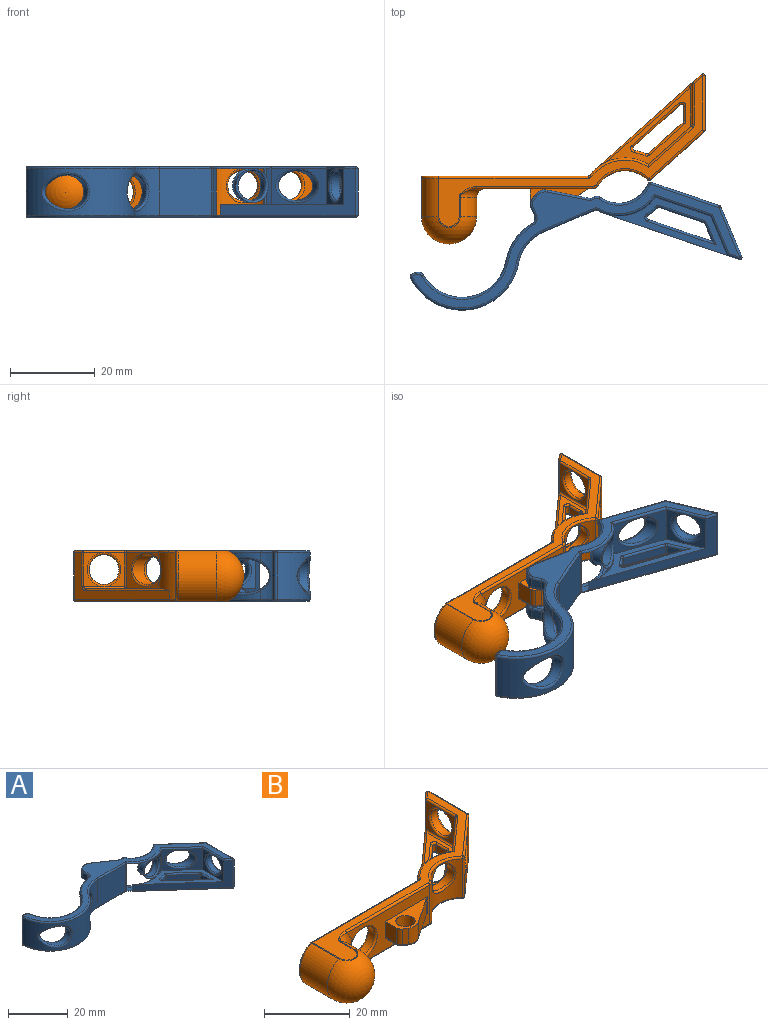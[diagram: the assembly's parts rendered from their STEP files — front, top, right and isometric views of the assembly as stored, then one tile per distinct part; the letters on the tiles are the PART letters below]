
ASSEMBLY  parts=2 mates=1
PART A: 142 faces, bbox 75.2x33.9x12.5 mm
  f0: plane 72.76x32.31mm, normal (0,0,-1), area 331.1mm2, adj f1,f2,f3,f4,f5,f6,f7,f8
  f1: torus R=12mm, axis (0,0,-1), area 2.2mm2, adj f0,f2,f7,f29
  f2: torus R=1mm, axis (0,0,-1), area 1.2mm2, adj f0,f1,f3,f30
  f3: cylinder r=0.5mm len=13.02mm, axis (0.75,-0.67,0), area 12.8mm2, adj f0,f2,f4,f31
  f4: cylinder r=0.5mm len=5.59mm, axis (0,1,0), area 3.8mm2, adj f0,f3,f5,f32
  f5: torus R=1mm, axis (0,0,-1), area 0.5mm2, adj f0,f4,f6,f33
  f6: cylinder r=0.5mm len=8.55mm, axis (-0.75,0.67,0), area 8.7mm2, adj f0,f5,f7,f34
  f7: torus R=1mm, axis (0,0,-1), area 0.6mm2, adj f0,f1,f6,f35
  f8: torus R=12.5mm, axis (0,0,-1), area 8.5mm2, adj f0,f9,f28,f36
  f9: torus R=2mm, axis (0,0,-1), area 1.9mm2, adj f0,f8,f10,f37
  f10: cylinder r=0.5mm len=2.34mm, axis (0,1,0), area 1.8mm2, adj f0,f9,f11,f38
  f11: torus R=1mm, axis (0,0,-1), area 1mm2, adj f0,f10,f12,f39
  f12: cylinder r=0.5mm len=1.44mm, axis (0.83,0.56,0), area 1.1mm2, adj f0,f11,f13,f40
  f13: torus R=2.5mm, axis (0,0,-1), area 2.6mm2, adj f0,f12,f14,f41
  f14: cylinder r=0.5mm len=8.86mm, axis (0.83,-0.56,0), area 8.1mm2, adj f0,f13,f15,f42
  f15: cylinder r=0.5mm len=1.22mm, axis (-1,0,0), area 0.9mm2, adj f0,f14,f16,f43
  f16: torus R=1mm, axis (0,0,-1), area 1.1mm2, adj f0,f15,f17,f44
  f17: torus R=8mm, axis (0,0,-1), area 10.8mm2, adj f0,f16,f45,f46
  f18: cylinder r=0.5mm len=13.04mm, axis (-0.75,0.67,0), area 13.4mm2, adj f0,f45,f47,f48
  f19: cylinder r=0.5mm len=12.75mm, axis (0,-1,0), area 10mm2, adj f0,f47,f49,f50
  f20: cylinder r=0.5mm len=25.33mm, axis (-0.75,0.67,0), area 26.3mm2, adj f0,f21,f49,f51
  f21: torus R=10mm, axis (0,0,-1), area 1.5mm2, adj f0,f20,f22,f52
  f22: torus R=1mm, axis (0,0,-1), area 0.5mm2, adj f0,f21,f23,f53
  f23: cylinder r=0.5mm len=13.18mm, axis (1,0,0), area 10.3mm2, adj f0,f22,f24,f54
  f24: torus R=10.5mm, axis (0,0,-1), area 7.9mm2, adj f0,f23,f25,f55
  f25: torus R=13mm, axis (0,0,-1), area 26.3mm2, adj f0,f24,f56,f57
  f26: cylinder r=0.5mm len=1.08mm, axis (-1,0,0), area 0.9mm2, adj f0,f27,f57,f58
  f27: torus R=1mm, axis (0,0,-1), area 1.5mm2, adj f0,f26,f28,f59
  f28: torus R=11mm, axis (0,0,-1), area 20.4mm2, adj f0,f8,f27,f60
  f29: cylinder r=12.5mm len=2.7mm, axis (0,0,1), area 5.7mm2, adj f1,f30,f35,f61
  f30: cylinder r=0.5mm len=2mm, axis (0,0,1), area 2.2mm2, adj f2,f29,f31,f62
  f31: plane 11.86x10.6mm, normal (0.67,0.75,0), area 31.8mm2, adj f3,f30,f32,f63
  f32: plane 4.47x2mm, normal (-1,0,0), area 8.9mm2, adj f4,f31,f33,f64
  f33: cylinder r=0.5mm len=2mm, axis (0,0,-1), area 0.8mm2, adj f5,f32,f34,f65
  f34: plane 8.21x7.35mm, normal (-0.67,-0.75,0), area 22mm2, adj f6,f33,f35,f66
  f35: cylinder r=0.5mm len=2mm, axis (0,0,1), area 1.1mm2, adj f7,f29,f34,f67
  f36: cylinder r=13mm len=11mm, axis (0,0,1), area 57.8mm2, adj f8,f37,f43,f60,f68,f69,f70,f71
  f37: cylinder r=1.5mm len=2.25mm, axis (0,0,1), area 4.8mm2, adj f9,f36,f38,f74
  f38: plane 2.34x2.25mm, normal (-1,0,0), area 5.3mm2, adj f10,f37,f39,f75
  f39: cylinder r=1.5mm len=2.25mm, axis (0,0,-1), area 3.3mm2, adj f11,f38,f40,f76
  f40: plane 2.25x1.16mm, normal (-0.56,0.83,0), area 3.1mm2, adj f12,f39,f41,f77
  f41: cylinder r=3mm len=3.37mm, axis (0,0,-1), area 8mm2, adj f13,f40,f42,f78
  f42: plane 8.45x5.73mm, normal (0.56,0.83,0), area 23mm2, adj f14,f41,f43,f79
  f43: plane 14.53x11.31mm, normal (0,1,0), area 84.3mm2, adj f15,f36,f42,f44,f72,f73,f79,f80
  f44: cylinder r=1.5mm len=11mm, axis (0,0,1), area 16.7mm2, adj f16,f43,f46,f83
  f45: sphere r=0.5mm, area 0.4mm2, adj f17,f18,f84
  f46: cylinder r=7.5mm len=11.64mm, axis (0,0,1), area -196.8mm2, adj f17,f44,f84,f85,f86
  f47: sphere r=0.5mm, area 0.3mm2, adj f18,f19,f87
  f48: plane 12.71x11.37mm, normal (0.67,0.75,0), area 120.1mm2, adj f18,f84,f87,f88,f89
  f49: sphere r=0.5mm, area 0.6mm2, adj f19,f20,f90
  f50: plane 12.75x11mm, normal (1,0,0), area 89.9mm2, adj f19,f87,f90,f91,f92
  f51: plane 24.99x22.35mm, normal (-0.67,-0.75,0), area 108.5mm2, adj f20,f52,f90,f93,f94,f95
  f52: cylinder r=10.5mm len=13.79mm, axis (0,0,1), area -189.1mm2, adj f21,f51,f53,f95,f96,f97,f98
  f53: cylinder r=0.5mm len=11mm, axis (0,0,1), area 5mm2, adj f22,f52,f54,f99
  f54: plane 13.18x11mm, normal (0,-1,0), area 145mm2, adj f23,f53,f55,f100
  f55: cylinder r=10mm len=11mm, axis (0,0,1), area 55.3mm2, adj f24,f54,f56,f101,f102
  f56: cylinder r=13.5mm len=24.74mm, axis (0,0,1), area 257.9mm2, adj f25,f55,f103,f104,f105,f106
  f57: sphere r=0.5mm, area 0.4mm2, adj f25,f26,f106
  f58: plane 11x1.08mm, normal (0,1,0), area 11.9mm2, adj f26,f59,f106,f107
  f59: cylinder r=1.5mm len=11mm, axis (0,0,1), area 18.2mm2, adj f27,f58,f60,f108,f109
  f60: cylinder r=10.5mm len=19.16mm, axis (0,0,1), area 177.8mm2, adj f28,f36,f59,f110,f111,f112
  f61: torus R=12mm, axis (0,0,-1), area 2.2mm2, adj f29,f62,f67,f95
  f62: torus R=1mm, axis (0,0,-1), area 1.2mm2, adj f30,f61,f63,f95
  f63: cylinder r=0.5mm len=13.02mm, axis (0.75,-0.67,0), area 12.8mm2, adj f31,f62,f64,f95
  f64: cylinder r=0.5mm len=5.59mm, axis (0,1,0), area 3.8mm2, adj f32,f63,f65,f95
  f65: torus R=1mm, axis (0,0,-1), area 0.5mm2, adj f33,f64,f66,f95
  f66: cylinder r=0.5mm len=8.55mm, axis (-0.75,0.67,0), area 8.7mm2, adj f34,f65,f67,f95
  f67: torus R=1mm, axis (0,0,-1), area 0.6mm2, adj f35,f61,f66,f95
  f68: bspline ~9.01x7.88mm, area 17.8mm2, adj f36,f110,f113
  f69: torus R=12.5mm, axis (0,0,-1), area 8.5mm2, adj f36,f111,f114,f115
  f70: cylinder r=1.5mm len=2.25mm, axis (0,0,1), area 4.8mm2, adj f36,f71,f114,f116
  f71: torus R=2mm, axis (0,0,-1), area 1.4mm2, adj f36,f70,f72,f117
  f72: plane 12.79x5.76mm, normal (0,0,-1), area 34.8mm2, adj f36,f43,f71,f80,f117,f118,f119,f120
  f73: plane 12.79x5.76mm, normal (0,0,1), area 34.8mm2, adj f36,f43,f74,f75,f76,f77,f78,f79
  f74: torus R=2mm, axis (0,0,-1), area 1.4mm2, adj f36,f37,f73,f75
  f75: cylinder r=0.5mm len=2.34mm, axis (0,-1,0), area 1.8mm2, adj f38,f73,f74,f76
  f76: torus R=1mm, axis (0,0,-1), area 1mm2, adj f39,f73,f75,f77
  f77: cylinder r=0.5mm len=1.44mm, axis (-0.83,-0.56,0), area 1.1mm2, adj f40,f73,f76,f78
  f78: torus R=2.5mm, axis (0,0,-1), area 2.6mm2, adj f41,f73,f77,f79
  f79: cylinder r=0.5mm len=8.73mm, axis (-0.83,0.56,0), area 7.7mm2, adj f42,f43,f73,f78
  f80: cylinder r=0.5mm len=8.73mm, axis (0.83,-0.56,0), area 7.7mm2, adj f43,f72,f81,f121
  f81: plane 8.45x5.73mm, normal (0.56,0.83,0), area 23mm2, adj f43,f80,f122,f123
  f82: cylinder r=0.5mm len=1.22mm, axis (1,0,0), area 0.9mm2, adj f43,f83,f115,f123
  f83: torus R=1mm, axis (0,0,-1), area 1.1mm2, adj f44,f82,f85,f115
  f84: cylinder r=0.5mm len=11mm, axis (0,0,1), area 8.3mm2, adj f45,f46,f48,f124
  f85: torus R=8mm, axis (0,0,-1), area 10.8mm2, adj f46,f83,f115,f124
  f86: bspline ~8.01x7.51mm, area 15.2mm2, adj f46,f125
  f87: cylinder r=0.5mm len=11mm, axis (0,0,-1), area 4.6mm2, adj f47,f48,f50,f126
  f88: cylinder r=0.5mm len=13.04mm, axis (0.75,-0.67,0), area 13.4mm2, adj f48,f115,f124,f126
  f89: bspline ~8x8mm, area 21.6mm2, adj f48,f127
  f90: cylinder r=0.5mm len=11mm, axis (0,0,-1), area 12.7mm2, adj f49,f50,f51,f128
  f91: cylinder r=0.5mm len=12.75mm, axis (0,-1,0), area 10mm2, adj f50,f115,f126,f128
  f92: torus R=4mm, axis (-1,0,0), area 18.2mm2, adj f50,f129
  f93: cylinder r=0.5mm len=2.5mm, axis (-0.75,0.67,0), area 2.2mm2, adj f51,f115,f128,f130
  f94: plane 10.06x8.5mm, normal (-1,0,0), area 35.3mm2, adj f51,f95,f98,f130,f131
  f95: plane 22.83x20.42mm, normal (0,0,1), area 80.6mm2, adj f51,f52,f61,f62,f63,f64,f65,f66
  f96: bspline ~8.41x8.01mm, area 21mm2, adj f52,f125
  f97: torus R=10mm, axis (0,0,-1), area 12mm2, adj f52,f99,f115,f132
  f98: plane 10.33x9.24mm, normal (-0.67,-0.75,0), area 50.3mm2, adj f52,f94,f95,f132,f133
  f99: torus R=1mm, axis (0,0,-1), area 0.5mm2, adj f53,f97,f100,f115
  f100: cylinder r=0.5mm len=13.18mm, axis (-1,0,0), area 10.3mm2, adj f54,f99,f102,f115
  f101: bspline ~9.02x6.25mm, area 15.6mm2, adj f55,f104,f113
  f102: torus R=10.5mm, axis (0,0,-1), area 7.9mm2, adj f55,f100,f105,f115
  f103: bspline ~9.35x9.01mm, area 27.5mm2, adj f56,f134
  f104: bspline ~8.92x4.77mm, area 7.4mm2, adj f56,f101,f113
  f105: torus R=13mm, axis (0,0,-1), area 26.3mm2, adj f56,f102,f115,f135
  f106: cylinder r=0.5mm len=11mm, axis (0,0,1), area 8.9mm2, adj f56,f57,f58,f135
  f107: cylinder r=0.5mm len=1.08mm, axis (1,0,0), area 0.9mm2, adj f58,f109,f115,f135
  f108: bspline ~4.61x1.41mm, area 2.6mm2, adj f59,f112,f134
  f109: torus R=1mm, axis (0,0,-1), area 1.5mm2, adj f59,f107,f111,f115
  f110: bspline ~7.48x3.01mm, area 9.2mm2, adj f60,f68,f113
  f111: torus R=11mm, axis (0,0,-1), area 20.4mm2, adj f60,f69,f109,f115
  f112: bspline ~10.01x9.01mm, area 20.8mm2, adj f60,f108,f134
  f113: cylinder r=4mm len=9.71mm, axis (0,-1,0), area 64.4mm2, adj f68,f101,f104,f110
  f114: torus R=2mm, axis (0,0,-1), area 1.9mm2, adj f69,f70,f115,f136
  f115: plane 72.76x32.31mm, normal (0,0,1), area 247.1mm2, adj f69,f82,f83,f85,f88,f91,f93,f97
  f116: plane 2.34x2.25mm, normal (-1,0,0), area 5.3mm2, adj f70,f117,f136,f140
  f117: cylinder r=0.5mm len=2.34mm, axis (0,1,0), area 1.8mm2, adj f71,f72,f116,f119
  f118: cylinder r=1.75mm len=5.5mm, axis (0,0,-1), area 60.5mm2, adj f72,f73
  f119: torus R=1mm, axis (0,0,-1), area 1mm2, adj f72,f117,f120,f140
  f120: cylinder r=0.5mm len=1.44mm, axis (0.83,0.56,0), area 1.1mm2, adj f72,f119,f121,f141
  f121: torus R=2.5mm, axis (0,0,-1), area 2.6mm2, adj f72,f80,f120,f122
  f122: cylinder r=3mm len=3.37mm, axis (0,0,-1), area 8mm2, adj f81,f121,f137,f141
  f123: cylinder r=0.5mm len=8.86mm, axis (-0.83,0.56,0), area 8.1mm2, adj f81,f82,f115,f137
  f124: sphere r=0.5mm, area 0.4mm2, adj f84,f85,f88
  f125: cylinder r=3.5mm len=7mm, axis (0,1,0), area 46.3mm2, adj f86,f96
  f126: sphere r=0.5mm, area 0.3mm2, adj f87,f88,f91
  f127: cylinder r=3.5mm len=9.89mm, axis (0,1,0), area 59mm2, adj f89,f133
  f128: sphere r=0.5mm, area 0.6mm2, adj f90,f91,f93
  f129: cylinder r=3.5mm len=7mm, axis (-1,0,0), area 44mm2, adj f92,f131
  f130: cylinder r=0.5mm len=10.29mm, axis (0,1,0), area 7.9mm2, adj f93,f94,f115,f132
  f131: torus R=4mm, axis (1,0,0), area 18.2mm2, adj f94,f129
  f132: cylinder r=0.5mm len=11.11mm, axis (-0.75,0.67,0), area 11.1mm2, adj f97,f98,f115,f130
  f133: bspline ~8x7.99mm, area 21.7mm2, adj f98,f127
  f134: cylinder r=4mm len=12.18mm, axis (0,1,0), area 79.7mm2, adj f103,f108,f112
  f135: sphere r=0.5mm, area 0.4mm2, adj f105,f106,f107
  f136: cylinder r=0.5mm len=2.34mm, axis (0,-1,0), area 1.8mm2, adj f114,f115,f116,f139
  f137: torus R=2.5mm, axis (0,0,-1), area 2.6mm2, adj f115,f122,f123,f138
  f138: cylinder r=0.5mm len=1.44mm, axis (-0.83,-0.56,0), area 1.1mm2, adj f115,f137,f139,f141
  f139: torus R=1mm, axis (0,0,-1), area 1mm2, adj f115,f136,f138,f140
  f140: cylinder r=1.5mm len=2.25mm, axis (0,0,-1), area 3.3mm2, adj f116,f119,f139,f141
  f141: plane 2.25x1.16mm, normal (-0.56,0.83,0), area 3.1mm2, adj f120,f122,f138,f140
PART B: 136 faces, bbox 67.4x40.1x19.8 mm
  f0: plane 8x4.81mm, normal (-1,0,0), area 13.3mm2, adj f121,f125,f126,f131
  f1: plane 2.1x0.7mm, normal (0,1,0), area 0.1mm2, adj f95,f96,f98
  f2: plane 2.1x0.7mm, normal (0,1,0), area 0.1mm2, adj f96,f105,f110
  f3: plane 31.25x11mm, normal (0,1,0), area 241.9mm2, adj f89,f97,f98,f106,f110,f113,f129
  f4: plane 19.61x18.18mm, normal (0,0,1), area 62.8mm2, adj f5,f24,f64,f65,f68,f69,f72,f73
  f5: cylinder r=10.5mm len=13.79mm, axis (0,0,1), area 81.9mm2, adj f4,f19,f24,f107,f113,f117,f128,f132
  f6: plane 12.71x11.37mm, normal (0.67,-0.75,0), area 120.1mm2, adj f22,f86,f102,f112,f134
  f7: cylinder r=7.5mm len=11.64mm, axis (0,0,1), area 99.1mm2, adj f35,f87,f102,f103,f133
  f8: plane 27.38x11.07mm, normal (0,-1,0), area 154.4mm2, adj f11,f13,f17,f18,f34,f35,f50,f54
  f9: plane 62.16x35.46mm, normal (0,0,-1), area 287.3mm2, adj f56,f57,f58,f60,f61,f62,f66,f67
  f10: plane 62.16x35.46mm, normal (0,0,1), area 202.3mm2, adj f83,f88,f90,f94,f99,f103,f104,f110
  f11: torus R=8.5mm, axis (0,-1,0), area 40.2mm2, adj f8,f38,f77,f78,f83
  f12: plane 4.5x1.16mm, normal (-0.56,-0.83,0), area 6.3mm2, adj f15,f18,f33,f52
  f13: plane 4.5x3.71mm, normal (-1,0,0), area 16.7mm2, adj f8,f18,f33,f50
  f14: plane 8.07x5.47mm, normal (0.56,-0.83,0), area 43.9mm2, adj f15,f18,f34,f54
  f15: cylinder r=3mm len=4.5mm, axis (0,0,1), area 16.1mm2, adj f12,f14,f18,f53
  f16: cylinder r=2.25mm len=5mm, axis (0,0,1), area 70.7mm2, adj f17,f18
  f17: plane 12.25x5.75mm, normal (0,0,-1), area 28.3mm2, adj f8,f16,f50,f51,f52,f53,f54
  f18: plane 14.1x6.25mm, normal (0,0,1), area 38mm2, adj f8,f12,f13,f14,f15,f16,f33,f34
  f19: plane 24.99x22.35mm, normal (-0.67,0.75,0), area 91.5mm2, adj f5,f20,f101,f120,f125,f127,f128
  f20: cylinder r=0.5mm len=11mm, axis (0,0,-1), area 12.7mm2, adj f19,f21,f92,f118
  f21: plane 12.75x11mm, normal (1,0,0), area 89.9mm2, adj f20,f22,f85,f116,f130
  f22: cylinder r=0.5mm len=11mm, axis (0,0,-1), area 4.6mm2, adj f6,f21,f81,f114
  f23: plane 8x4.81mm, normal (-1,0,0), area 13.3mm2, adj f121,f124,f126,f131
  f24: plane 10.18x9.11mm, normal (-0.67,0.75,0), area 48.4mm2, adj f4,f5,f119,f124,f126,f135
  f25: cylinder r=3.5mm len=9.89mm, axis (0,1,0), area 59mm2, adj f134,f135
  f26: cylinder r=3.5mm len=7mm, axis (0,1,0), area 46.2mm2, adj f132,f133
  f27: cylinder r=3.5mm len=7mm, axis (-1,0,0), area 44mm2, adj f130,f131
  f28: cylinder r=4mm len=8mm, axis (0,-1,0), area 50.7mm2, adj f76,f77,f129
  f29: plane 3.35x2mm, normal (-1,0,0), area 6.7mm2, adj f59,f60,f69,f70
  f30: plane 11.02x9.86mm, normal (0.67,-0.75,0), area 29.6mm2, adj f61,f70,f71,f75
  f31: cylinder r=12.5mm len=2.7mm, axis (0,0,1), area 5.7mm2, adj f62,f63,f71,f72
  f32: plane 8.21x7.35mm, normal (-0.67,0.75,0), area 22mm2, adj f56,f59,f63,f64
  f33: cylinder r=1.5mm len=4.5mm, axis (0,0,-1), area 6.6mm2, adj f12,f13,f18,f51
  f34: cylinder r=1.5mm len=4.5mm, axis (0,0,1), area 4mm2, adj f8,f14,f18,f55
  f35: cylinder r=1.5mm len=11mm, axis (0,0,1), area 16.7mm2, adj f7,f8,f82,f94
  f36: cylinder r=6.5mm len=11.92mm, axis (0,1,0), area 135.7mm2, adj f37,f91,f96,f104
  f37: sphere r=6.5mm, area 243.3mm2, adj f36,f38,f84,f99
  f38: cylinder r=6.5mm len=11.92mm, axis (0,1,0), area 67.8mm2, adj f11,f37,f80,f90
  f39: cylinder r=5.5mm len=9mm, axis (0,1,0), area 91.8mm2, adj f40,f46,f47,f96
  f40: sphere r=5.5mm, area 152.1mm2, adj f39,f41,f45,f48
  f41: cylinder r=5.5mm len=9mm, axis (0,1,0), area 91.8mm2, adj f40,f44,f49,f97
  f42: plane 10.5x3mm, normal (0,0,-1), area 30.5mm2, adj f44,f45,f46,f110
  f43: plane 10.5x3mm, normal (0,0,1), area 30.5mm2, adj f47,f48,f49,f98
  f44: cylinder r=3mm len=9mm, axis (0,1,0), area 17.4mm2, adj f41,f42,f45,f106
  f45: torus R=1.5mm, axis (0,0,-1), area 14.8mm2, adj f40,f42,f44,f46
  f46: cylinder r=3mm len=9mm, axis (0,1,0), area 17.4mm2, adj f39,f42,f45,f105
  f47: cylinder r=3mm len=9mm, axis (0,1,0), area 17.4mm2, adj f39,f43,f48,f95
  f48: torus R=1.5mm, axis (0,0,-1), area 14.8mm2, adj f40,f43,f47,f49
  f49: cylinder r=3mm len=9mm, axis (0,1,0), area 17.4mm2, adj f41,f43,f48,f89
  f50: cylinder r=0.5mm len=3.71mm, axis (0,-1,0), area 2.9mm2, adj f8,f13,f17,f51
  f51: torus R=1mm, axis (0,0,-1), area 1mm2, adj f17,f33,f50,f52
  f52: cylinder r=0.5mm len=1.44mm, axis (0.83,-0.56,0), area 1.1mm2, adj f12,f17,f51,f53
  f53: torus R=2.5mm, axis (0,0,-1), area 2.6mm2, adj f15,f17,f52,f54
  f54: cylinder r=0.5mm len=8.35mm, axis (0.83,0.56,0), area 7.6mm2, adj f8,f14,f17,f53,f55
  f55: torus R=2mm, axis (0,0,-1), area 0.3mm2, adj f8,f34,f54
  f56: cylinder r=0.5mm len=8.55mm, axis (0.75,0.67,0), area 8.7mm2, adj f9,f32,f57,f58
  f57: torus R=1mm, axis (0,0,-1), area 0.5mm2, adj f9,f56,f59,f60
  f58: torus R=1mm, axis (0,0,-1), area 0.6mm2, adj f9,f56,f62,f63
  f59: cylinder r=0.5mm len=2mm, axis (0,0,-1), area 0.8mm2, adj f29,f32,f57,f65
  f60: cylinder r=0.5mm len=3.35mm, axis (0,1,0), area 2.6mm2, adj f9,f29,f57,f66
  f61: cylinder r=0.5mm len=11.36mm, axis (-0.75,-0.67,0), area 11.6mm2, adj f9,f30,f66,f67
  f62: torus R=12mm, axis (0,0,-1), area 2.2mm2, adj f9,f31,f58,f67
  f63: cylinder r=0.5mm len=2mm, axis (0,0,1), area 1.1mm2, adj f31,f32,f58,f68
  f64: cylinder r=0.5mm len=8.55mm, axis (0.75,0.67,0), area 8.7mm2, adj f4,f32,f65,f68
  f65: torus R=1mm, axis (0,0,-1), area 0.5mm2, adj f4,f59,f64,f69
  f66: torus R=1mm, axis (0,0,-1), area 1.2mm2, adj f9,f60,f61,f70
  f67: torus R=1mm, axis (0,0,-1), area 1.2mm2, adj f9,f61,f62,f71
  f68: torus R=1mm, axis (0,0,-1), area 0.6mm2, adj f4,f63,f64,f72
  f69: cylinder r=0.5mm len=3.35mm, axis (0,1,0), area 2.6mm2, adj f4,f29,f65,f73
  f70: cylinder r=0.5mm len=2mm, axis (0,0,-1), area 2.3mm2, adj f29,f30,f66,f73
  f71: cylinder r=0.5mm len=2mm, axis (0,0,1), area 2.2mm2, adj f30,f31,f67,f74
  f72: torus R=12mm, axis (0,0,-1), area 2.2mm2, adj f4,f31,f68,f74
  f73: torus R=1mm, axis (0,0,-1), area 1.2mm2, adj f4,f69,f70,f75
  f74: torus R=1mm, axis (0,0,-1), area 1.2mm2, adj f4,f71,f72,f75
  f75: cylinder r=0.5mm len=11.36mm, axis (-0.75,-0.67,0), area 11.6mm2, adj f4,f30,f73,f74
  f76: torus R=4.5mm, axis (0,-1,0), area 17.1mm2, adj f8,f28,f77
  f77: bspline ~5.2x1.17mm, area 3mm2, adj f11,f28,f76
  f78: bspline ~4.93x2.56mm, area 2.4mm2, adj f9,f11,f79,f80
  f79: cylinder r=0.5mm len=27.31mm, axis (1,0,0), area 21.5mm2, adj f8,f9,f78,f82
  f80: cylinder r=0.5mm len=4.5mm, axis (0,1,0), area 0.9mm2, adj f9,f38,f78,f84
  f81: sphere r=0.5mm, area 0.2mm2, adj f22,f85,f86
  f82: torus R=1mm, axis (0,0,-1), area 1.1mm2, adj f9,f35,f79,f87
  f83: bspline ~4.93x2.56mm, area 2.4mm2, adj f10,f11,f88,f90
  f84: torus R=2.4mm, axis (0,0,-1), area 1.6mm2, adj f9,f37,f80,f91
  f85: cylinder r=0.5mm len=12.75mm, axis (0,-1,0), area 10mm2, adj f9,f21,f81,f92
  f86: cylinder r=0.5mm len=13.04mm, axis (0.75,0.67,0), area 13.4mm2, adj f6,f9,f81,f93
  f87: torus R=8mm, axis (0,0,-1), area 10.8mm2, adj f7,f9,f82,f93
  f88: cylinder r=0.5mm len=27.31mm, axis (-1,0,0), area 21.5mm2, adj f8,f10,f83,f94
  f89: torus R=3.5mm, axis (0,-1,0), area 1.6mm2, adj f3,f49,f97,f98
  f90: cylinder r=0.5mm len=4.5mm, axis (0,1,0), area 0.9mm2, adj f10,f38,f83,f99
  f91: cylinder r=0.5mm len=9mm, axis (0,1,0), area 1.9mm2, adj f9,f36,f84,f100
  f92: sphere r=0.5mm, area 0.6mm2, adj f20,f85,f101
  f93: sphere r=0.5mm, area 0.4mm2, adj f86,f87,f102
  f94: torus R=1mm, axis (0,0,-1), area 1.1mm2, adj f10,f35,f88,f103
  f95: torus R=3.5mm, axis (0,-1,0), area 1.6mm2, adj f1,f47,f96,f98
  f96: torus R=6mm, axis (0,-1,0), area 19.8mm2, adj f1,f2,f36,f39,f95,f100,f105,f109
  f97: torus R=6mm, axis (0,-1,0), area 8.3mm2, adj f3,f41,f89,f106
  f98: cylinder r=0.5mm len=35.15mm, axis (1,0,0), area 30mm2, adj f1,f3,f9,f43,f89,f95,f100,f111
  f99: torus R=2.4mm, axis (0,0,-1), area 1.6mm2, adj f10,f37,f90,f104
  f100: sphere r=0.5mm, area 0.1mm2, adj f91,f96,f98
  f101: cylinder r=0.5mm len=25.33mm, axis (0.75,0.67,0), area 26.3mm2, adj f9,f19,f92,f107
  f102: cylinder r=0.5mm len=11mm, axis (0,0,1), area 8.3mm2, adj f6,f7,f93,f108
  f103: torus R=8mm, axis (0,0,-1), area 10.8mm2, adj f7,f10,f94,f108
  f104: cylinder r=0.5mm len=9mm, axis (0,1,0), area 1.9mm2, adj f10,f36,f99,f109
  f105: torus R=3.5mm, axis (0,-1,0), area 1.6mm2, adj f2,f46,f96,f110
  f106: torus R=3.5mm, axis (0,-1,0), area 1.6mm2, adj f3,f44,f97,f110
  f107: torus R=10mm, axis (0,0,-1), area 1.5mm2, adj f5,f9,f101,f111
  f108: sphere r=0.5mm, area 0.5mm2, adj f102,f103,f112
  f109: sphere r=0.5mm, area 0.1mm2, adj f96,f104,f110
  f110: cylinder r=0.5mm len=35.15mm, axis (-1,0,0), area 30mm2, adj f2,f3,f10,f42,f105,f106,f109,f115
  f111: torus R=1mm, axis (0,0,-1), area 0.5mm2, adj f9,f98,f107,f113
  f112: cylinder r=0.5mm len=13.04mm, axis (-0.75,-0.67,0), area 13.4mm2, adj f6,f10,f108,f114
  f113: cylinder r=0.5mm len=11mm, axis (0,0,1), area 5mm2, adj f3,f5,f111,f115
  f114: sphere r=0.5mm, area 0.2mm2, adj f22,f112,f116
  f115: torus R=1mm, axis (0,0,-1), area 0.5mm2, adj f10,f110,f113,f117
  f116: cylinder r=0.5mm len=12.75mm, axis (0,-1,0), area 10mm2, adj f10,f21,f114,f118
  f117: torus R=10mm, axis (0,0,-1), area 12mm2, adj f5,f10,f115,f119
  f118: sphere r=0.5mm, area 0.5mm2, adj f20,f116,f120
  f119: cylinder r=0.5mm len=10.78mm, axis (0.75,0.67,0), area 10.9mm2, adj f10,f24,f117,f122
  f120: cylinder r=0.5mm len=2.33mm, axis (-0.75,-0.67,0), area 2.1mm2, adj f10,f19,f118,f123
  f121: cylinder r=0.5mm len=9.62mm, axis (0,1,0), area 7.6mm2, adj f0,f10,f23,f122,f123
  f122: torus R=1mm, axis (0,0,-1), area 0.5mm2, adj f10,f119,f121,f124
  f123: sphere r=0.5mm, area 0.2mm2, adj f120,f121,f125
  f124: cylinder r=0.5mm len=8.37mm, axis (0,0,-1), area 3.4mm2, adj f23,f24,f122,f126
  f125: cylinder r=0.5mm len=8mm, axis (0,0,1), area 3.4mm2, adj f0,f19,f123,f127
  f126: cylinder r=0.5mm len=10.29mm, axis (0,1,0), area 7.6mm2, adj f0,f4,f23,f24,f124,f127
  f127: bspline ~1.42x1.17mm, area 0.8mm2, adj f19,f125,f126,f128
  f128: cylinder r=0.5mm len=22.33mm, axis (-0.75,-0.67,0), area 21.9mm2, adj f4,f5,f19,f127
  f129: torus R=4.5mm, axis (0,-1,0), area 20.6mm2, adj f3,f28
  f130: torus R=4mm, axis (-1,0,0), area 18.2mm2, adj f21,f27
  f131: torus R=4mm, axis (1,0,0), area 18.2mm2, adj f0,f23,f27
  f132: bspline ~8.41x8.01mm, area 21mm2, adj f5,f26
  f133: bspline ~8.01x7.51mm, area 15.2mm2, adj f7,f26
  f134: bspline ~8x7.99mm, area 21.7mm2, adj f6,f25
  f135: bspline ~8x8mm, area 21.6mm2, adj f24,f25
PLACE A rot(axis=(0,0,1),23deg) t=(-19.92,-6.15,-3.25)mm
PLACE B t=(-22.59,2.5,-3.25)mm fixed
MATE revolute A.f13 <-> B.f15  axis (0,0,-1) through (0,4.75,-9.75)mm
